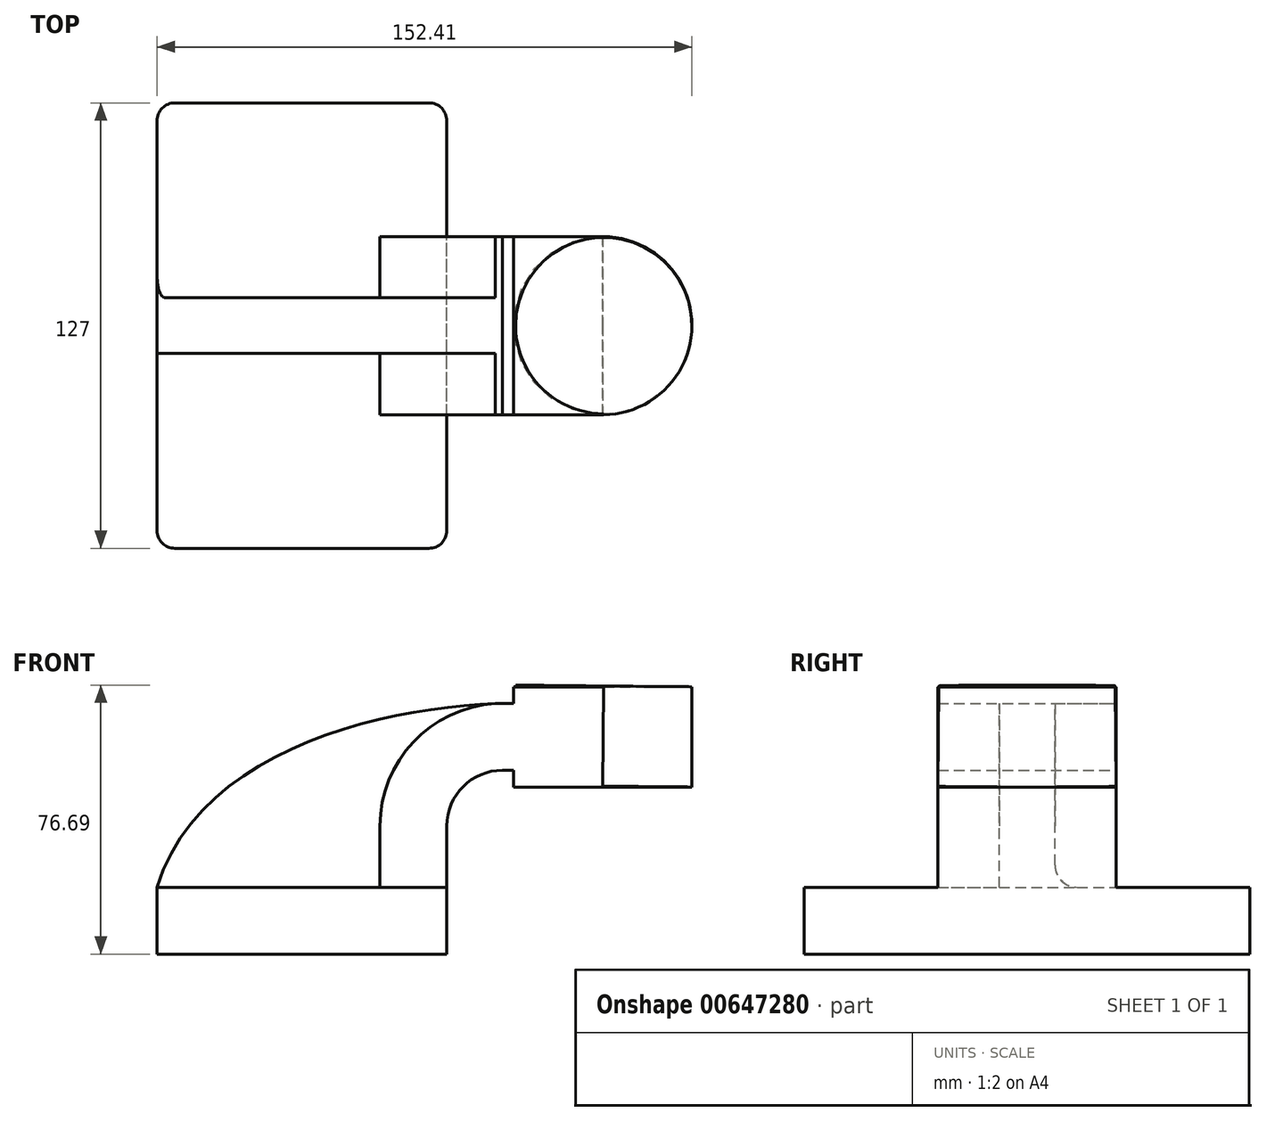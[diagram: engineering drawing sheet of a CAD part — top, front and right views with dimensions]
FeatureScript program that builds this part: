
annotation { "Feature Type Name" : "Feature", "Feature Type Description" : "" }
export const myFeature = defineFeature(function(context is Context, id is Id, definition is map)
    precondition{}
    {
        {
            var Q0;
            Q0=qCreatedBy(makeId("Front.planeOp"),FACE);
            var sketch = newSketch(context, id + "F0", { "sketchPlane" : qUnion([Q0])});
            skLineSegment(sketch, "E0.bottom", {"start": v(41.28, -9.52) * mm, "end": v(-41.28, -9.52) * mm});
            skLineSegment(sketch, "E0.top", {"start": v(41.28, 9.53) * mm, "end": v(-41.28, 9.53) * mm});
            skLineSegment(sketch, "E0.left", {"start": v(41.28, -9.52) * mm, "end": v(41.28, 9.53) * mm});
            skLineSegment(sketch, "E0.right", {"start": v(-41.28, -9.52) * mm, "end": v(-41.28, 9.53) * mm});
            skPoint(sketch, "E0.middle", {"position": v(0, 0) * mm});
            skLineSegment(sketch, "E1.bottom", {"start": v(111.12, 38.1) * mm, "end": v(60.32, 38.1) * mm});
            skLineSegment(sketch, "E1.top", {"start": v(111.12, 66.68) * mm, "end": v(60.32, 66.68) * mm});
            skLineSegment(sketch, "E1.left", {"start": v(111.12, 38.1) * mm, "end": v(111.12, 66.68) * mm});
            skLineSegment(sketch, "E1.right", {"start": v(60.32, 38.1) * mm, "end": v(60.32, 66.68) * mm});
            skPoint(sketch, "E1.middle", {"position": v(85.72, 52.39) * mm});
            skLineSegment(sketch, "E2", {"start": v(41.28, 9.53) * mm, "end": v(41.28, 27) * mm});
            skArc(sketch, "E3", {"start": v(41.27, 27) * mm, "mid": v(45.92, 38.23) * mm, "end": v(57.15, 42.88) * mm});
            skLineSegment(sketch, "E4", {"start": v(57.15, 42.88) * mm, "end": v(86, 42.88) * mm});
            skLineSegment(sketch, "E5.0", {"start": v(57.15, 61.93) * mm, "end": v(86, 61.93) * mm});
            skArc(sketch, "E5.1", {"start": v(22.23, 27) * mm, "mid": v(32.45, 51.7) * mm, "end": v(57.15, 61.93) * mm});
            skLineSegment(sketch, "E5.2", {"start": v(22.22, 9.53) * mm, "end": v(22.22, 27) * mm});
            skFitSpline(sketch, "E6", {"points": [v(-41.28, 9.52) * mm, v(57.15, 61.93) * mm], "startDerivative": vector(36.98, 120.5) * mm, "endDerivative": vector(95.64, 2.24) * mm});
            skLineSegment(sketch, "E7", {"start": v(85.72, 38.1) * mm, "end": v(86, 66.68) * mm});
            skSolve(sketch);
        }
        {
            var Q0;
            Q0=makeQuery(id+"F0.imprint","IMPRINT",FACE,{"disambiguationData":[TD([[makeQuery(id+"F0.imprint","IMPRINT",EDGE,{"derivedFrom":sQuery(id+"F0.wireOp",EDGE,"E0.bottom")}),-1.0]])]});
            extrude(context, id + "F1", {"entities" : qUnion([Q0]), "endBound" : BoundingType.SYMMETRIC, "depth" : 127 * mm, "offsetDistance" : 25.4 * mm});
        }
        {
            var Q0;
            {var subQ1=sQuery(id+"F0.wireOp",EDGE,"E2");Q0=makeQuery(id+"F0.imprint","IMPRINT",FACE,{"disambiguationData":[TD([[makeQuery(id+"F0.imprint","IMPRINT",EDGE,{"derivedFrom":subQ1}),1.0]])]});}
            extrude(context, id + "F2", {"entities" : qUnion([Q0]), "operationType" : NewBodyOperationType.ADD, "endBound" : BoundingType.SYMMETRIC, "depth" : 50.8 * mm, "offsetDistance" : 25.4 * mm});
        }
        {
            var Q0;
            {var subQ0=sQuery(id+"F0.wireOp",EDGE,"E1.right");var subQ1=sQuery(id+"F0.wireOp",EDGE,"E1.top");var subQ2=makeQuery(id+"F0.imprint","INTERSECT",VERTEX,{"derivedFrom":[subQ1,subQ0]});Q0=makeQuery(id+"F0.imprint","IMPRINT",FACE,{"disambiguationData":[TD([[makeQuery(id+"F0.imprint","IMPRINT",EDGE,{"disambiguationData":[TD([[subQ2,1.0]])],"derivedFrom":subQ1}),1.0]])]});}
            var Q1;
            {var subQ0=sQuery(id+"F0.wireOp",EDGE,"E4");var subQ1=sQuery(id+"F0.wireOp",EDGE,"E1.right");var subQ2=makeQuery(id+"F0.imprint","INTERSECT",VERTEX,{"derivedFrom":[subQ1,subQ0]});Q1=makeQuery(id+"F0.imprint","IMPRINT",FACE,{"disambiguationData":[TD([[makeQuery(id+"F0.imprint","IMPRINT",EDGE,{"disambiguationData":[TD([[subQ2,-1.0]])],"derivedFrom":subQ1}),-1.0]])]});}
            var Q2;
            {var subQ0=sQuery(id+"F0.wireOp",EDGE,"E1.right");var subQ1=sQuery(id+"F0.wireOp",EDGE,"E1.bottom");var subQ2=makeQuery(id+"F0.imprint","INTERSECT",VERTEX,{"derivedFrom":[subQ1,subQ0]});Q2=makeQuery(id+"F0.imprint","IMPRINT",FACE,{"disambiguationData":[TD([[makeQuery(id+"F0.imprint","IMPRINT",EDGE,{"disambiguationData":[TD([[subQ2,1.0]])],"derivedFrom":subQ1}),-1.0]])]});}
            extrude(context, id + "F3", {"entities" : qUnion([Q0, Q1, Q2]), "operationType" : NewBodyOperationType.ADD, "endBound" : BoundingType.SYMMETRIC, "depth" : 50.8 * mm, "offsetDistance" : 25.4 * mm});
        }
        {
            var Q0;
            {var subQ3=sQuery(id+"F0.wireOp",EDGE,"E5.2");Q0=makeQuery(id+"F0.imprint","IMPRINT",FACE,{"disambiguationData":[TD([[makeQuery(id+"F0.imprint","IMPRINT",EDGE,{"derivedFrom":subQ3}),1.0]])]});}
            extrude(context, id + "F4", {"entities" : qUnion([Q0]), "operationType" : NewBodyOperationType.ADD, "endBound" : BoundingType.SYMMETRIC, "depth" : 15.88 * mm, "offsetDistance" : 25.4 * mm});
        }
        {
            var Q0;
            {var subQ4=sQuery(id+"F0.wireOp",EDGE,"E1.left");Q0=makeQuery(id+"F0.imprint","IMPRINT",FACE,{"disambiguationData":[TD([[makeQuery(id+"F0.imprint","IMPRINT",EDGE,{"derivedFrom":subQ4}),1.0]])]});}
            var Q1;
            Q1=sQuery(id+"F0.wireOp",EDGE,"E7");
            revolve(context, id + "F5", {"operationType" : NewBodyOperationType.ADD, "entities" : qUnion([Q0]), "axis" : qUnion([Q1]), "revolveType" : RevolveType.FULL});
        }
        {
            var Q0;
            Q0=makeQuery(id+"F1.opExtrude","CAP_EDGE",EDGE,{"disambiguationData":[OSD([sQuery(id+"F0.wireOp",EDGE,"E0.left")])],"isStart":false});
            var Q1;
            Q1=makeQuery(id+"F1.opExtrude","CAP_EDGE",EDGE,{"disambiguationData":[OSD([sQuery(id+"F0.wireOp",EDGE,"E0.right")])],"isStart":false});
            var Q2;
            Q2=makeQuery(id+"F1.opExtrude","CAP_EDGE",EDGE,{"disambiguationData":[OSD([sQuery(id+"F0.wireOp",EDGE,"E0.left")])],"isStart":true});
            var Q3;
            Q3=makeQuery(id+"F1.opExtrude","CAP_EDGE",EDGE,{"disambiguationData":[OSD([sQuery(id+"F0.wireOp",EDGE,"E0.right")])],"isStart":true});
            fillet(context, id + "F6", {"entities" : qUnion([Q0, Q1, Q2, Q3]), "radius" : 5.08 * mm, "tangentPropagation" : true, "allowEdgeOverflow" : false});
        }
        {
            var Q0;
            Q0=makeQuery(id+"F4.opExtrude","CAP_EDGE",EDGE,{"disambiguationData":[OSD([sQuery(id+"F0.wireOp",EDGE,"E0.top")])],"isStart":true});
            var Q1;
            Q1=makeQuery(id+"F4.opExtrude","CAP_EDGE",EDGE,{"disambiguationData":[OSD([sQuery(id+"F0.wireOp",EDGE,"E0.top")])],"isStart":false});
            fillet(context, id + "F7", {"entities" : qUnion([Q0, Q1]), "radius" : 6.35 * mm, "tangentPropagation" : true, "allowEdgeOverflow" : false});
        }
    });
